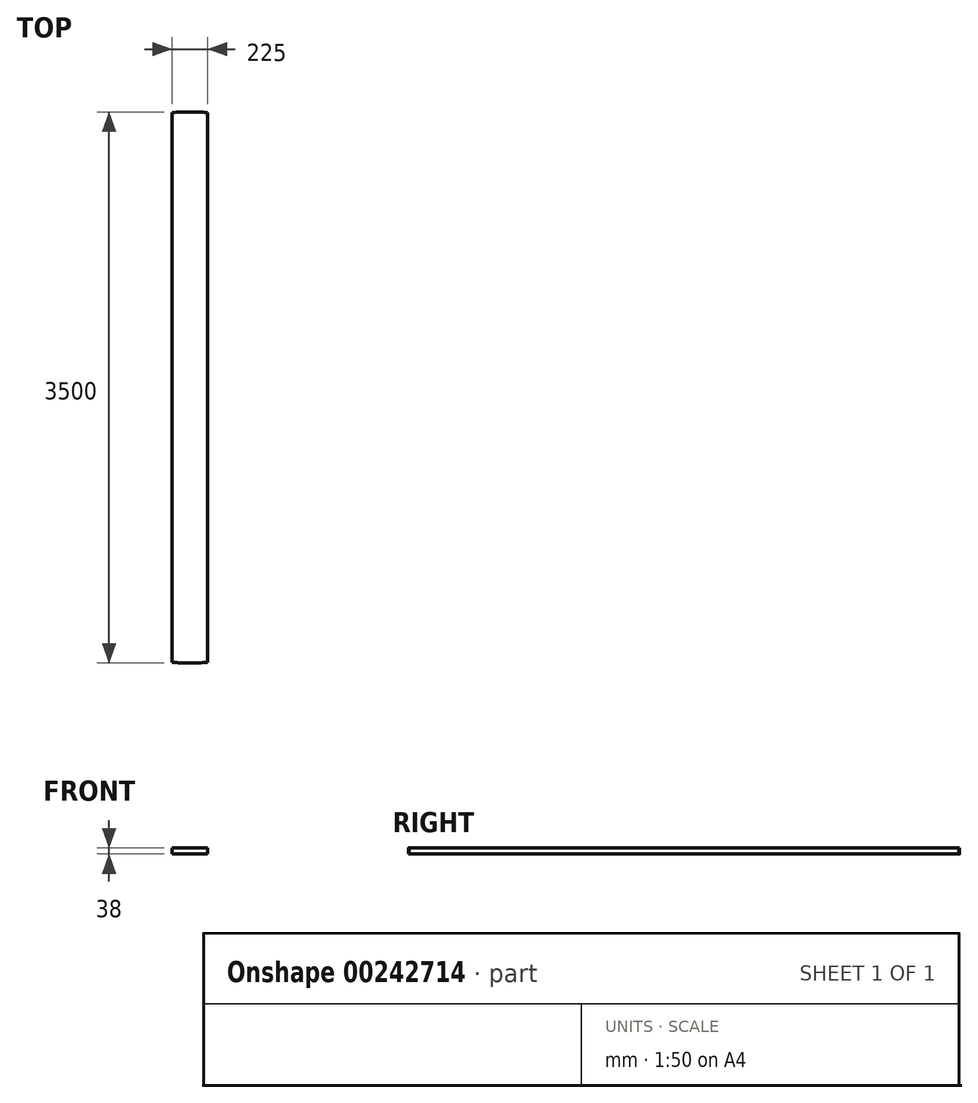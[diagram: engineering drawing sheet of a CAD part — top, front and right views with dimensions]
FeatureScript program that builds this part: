
annotation { "Feature Type Name" : "Feature", "Feature Type Description" : "" }
export const myFeature = defineFeature(function(context is Context, id is Id, definition is map)
    precondition{}
    {
        {
            var Q0;
            Q0=qCreatedBy(makeId("Top.planeOp"),FACE);
            var sketch = newSketch(context, id + "F0", { "sketchPlane" : qUnion([Q0])});
            skLineSegment(sketch, "E0.bottom", {"start": v(-111.56, 3649.74) * mm, "end": v(113.44, 3649.74) * mm});
            skLineSegment(sketch, "E0.top", {"start": v(-111.56, -350.26) * mm, "end": v(113.44, -350.26) * mm});
            skLineSegment(sketch, "E0.left", {"start": v(-111.56, 3649.74) * mm, "end": v(-111.56, -350.26) * mm});
            skLineSegment(sketch, "E0.right", {"start": v(113.44, 3649.74) * mm, "end": v(113.44, -350.26) * mm});
            skCircle(sketch, "E1", {"center": v(0, 1649.74) * mm, "radius": 1750 * mm});
            skPoint(sketch, "E1.centerSnap0", {"position": v(113.44, 1649.74) * mm});
            skSolve(sketch);
        }
        {
            var Q0;
            Q0 = qSketchRegion(id + "F2", true);
            var Q1;
            {var subQ0=sQuery(id+"F0.wireOp",EDGE,"E1");var subQ1=sQuery(id+"F0.wireOp",EDGE,"E0.left");var subQ2=makeQuery(id+"F0.imprint","INTERSECT",VERTEX,{"disambiguationData":[OD(0.0)],"derivedFrom":[subQ1,subQ0]});Q1=makeQuery(id+"F0.imprint","IMPRINT",FACE,{"disambiguationData":[TD([[makeQuery(id+"F0.imprint","IMPRINT",EDGE,{"disambiguationData":[TD([[subQ2,-1.0]])],"derivedFrom":subQ1}),1.0]])]});}
            extrude(context, id + "F1", {"entities" : qUnion([Q0, Q1]), "depth" : 38 * mm});
        }
    });
